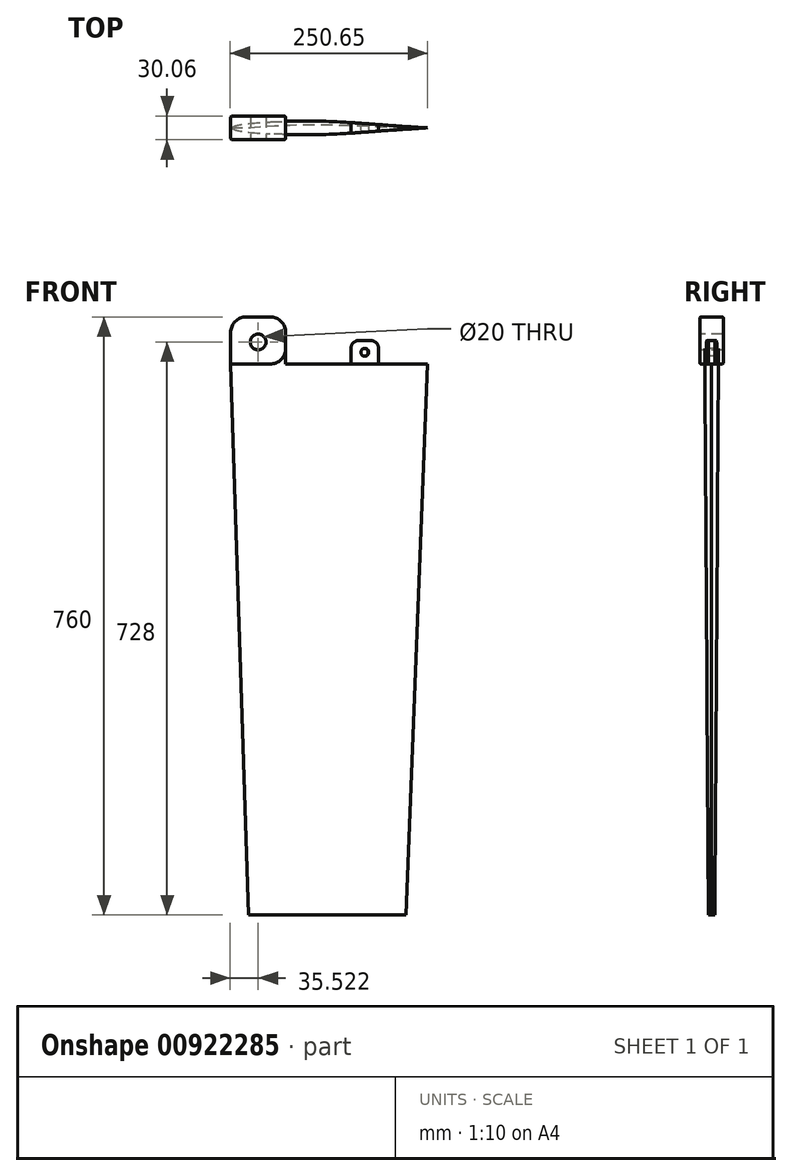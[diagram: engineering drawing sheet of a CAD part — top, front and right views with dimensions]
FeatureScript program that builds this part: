
annotation { "Feature Type Name" : "Feature", "Feature Type Description" : "" }
export const myFeature = defineFeature(function(context is Context, id is Id, definition is map)
    precondition{}
    {
        {
            var Q0;
            Q0=qCreatedBy(makeId("Top.planeOp"),FACE);
            var sketch = newSketch(context, id + "F0", { "sketchPlane" : qUnion([Q0])});
            skLineSegment(sketch, "E0", {"start": v(-132.78, 0) * mm, "end": v(117.22, 0) * mm});
            skFitSpline(sketch, "E1", {"points": [v(-132.78, 0) * mm, v(-121.8, 3.87) * mm, v(-98.61, 6.61) * mm, v(-16.83, 8.44) * mm, v(117.22, 0) * mm], "startDerivative": vector(116.96, 62.15) * mm, "endDerivative": vector(499.98, -28.84) * mm});
            skSolve(sketch);
        }
        {
            var Q0;
            Q0=qCreatedBy(makeId("Top.planeOp"),FACE);
            cPlane(context, id + "F1", {"entities" : qUnion([Q0]), "cplaneType" : CPlaneType.OFFSET, "offset" : 700 * mm, "oppositeDirection" : true, "width" : 150 * mm, "height" : 150 * mm});
        }
        {
            var Q0;
            Q0=qCreatedBy(id+"F1.planeOp",FACE);
            var sketch = newSketch(context, id + "F2", { "sketchPlane" : qUnion([Q0])});
            skLineSegment(sketch, "E2", {"start": v(-110.06, 0) * mm, "end": v(89.94, 0) * mm});
            skFitSpline(sketch, "E3", {"points": [v(-110.06, 0) * mm, v(-86.84, 2.4) * mm, v(-18.9, 4.12) * mm, v(30.9, 2.84) * mm, v(89.94, 0) * mm], "startDerivative": vector(17.15, 11.43) * mm, "endDerivative": vector(201.05, -10.2) * mm});
            skSolve(sketch);
        }
        {
            var Q0;
            Q0=makeQuery(id+"F0.imprint","IMPRINT",FACE,{"disambiguationData":[TD([[makeQuery(id+"F0.imprint","IMPRINT",EDGE,{"derivedFrom":sQuery(id+"F0.wireOp",EDGE,"E0")}),1.0]])]});
            var Q1;
            Q1=makeQuery(id+"F2.imprint","IMPRINT",FACE,{"disambiguationData":[TD([[makeQuery(id+"F2.imprint","IMPRINT",EDGE,{"derivedFrom":sQuery(id+"F2.wireOp",EDGE,"E2")}),1.0]])]});
            loft(context, id + "F3", {"sheetProfilesArray" : [{ "sheetProfileEntities" : qUnion([Q0]) }, { "sheetProfileEntities" : qUnion([Q1]) }]});
        }
        {
            var Q0;
            Q0=makeQuery(id+"F3.opLoft","SWEPT_BODY",BODY,{"disambiguationData":[OSD([makeQuery(id+"F0.imprint","IMPRINT",FACE,{"disambiguationData":[TD([[makeQuery(id+"F0.imprint","IMPRINT",EDGE,{"derivedFrom":sQuery(id+"F0.wireOp",EDGE,"E0")}),1.0]])]}),makeQuery(id+"F2.imprint","IMPRINT",FACE,{"disambiguationData":[TD([[makeQuery(id+"F2.imprint","IMPRINT",EDGE,{"derivedFrom":sQuery(id+"F2.wireOp",EDGE,"E2")}),1.0]])]})])]});
            var Q1;
            {var subQ0=sQuery(id+"F2.wireOp",EDGE,"E2");var subQ1=sQuery(id+"F2.wireOp",EDGE,"E3");var subQ2=sQuery(id+"F0.wireOp",EDGE,"E0");var subQ3=sQuery(id+"F0.wireOp",EDGE,"E1");Q1=makeQuery(id+"F3.opLoft","SWEPT_FACE",FACE,{"disambiguationData":[OSD([subQ2,subQ3,subQ0,subQ1]),TDD([makeQuery(id+"F0.imprint","INTERSECT",VERTEX,{"disambiguationData":[OD(0.0)],"derivedFrom":[subQ2,subQ3]}),makeQuery(id+"F0.imprint","INTERSECT",VERTEX,{"disambiguationData":[OD(1.0)],"derivedFrom":[subQ2,subQ3]}),makeQuery(id+"F0.imprint","IMPRINT",EDGE,{"derivedFrom":subQ2}),makeQuery(id+"F2.imprint","INTERSECT",VERTEX,{"disambiguationData":[OD(0.0)],"derivedFrom":[subQ0,subQ1]}),makeQuery(id+"F2.imprint","INTERSECT",VERTEX,{"disambiguationData":[OD(1.0)],"derivedFrom":[subQ0,subQ1]}),makeQuery(id+"F2.imprint","IMPRINT",EDGE,{"derivedFrom":subQ0})])]});}
            mirror(context, id + "F4", {"operationType" : NewBodyOperationType.ADD, "entities" : qUnion([Q0]), "mirrorPlane" : qUnion([Q1])});
        }
        {
            var Q0;
            {var subQ0=makeQuery(id+"F3.opLoft","CAP_FACE",FACE,{"disambiguationData":[OSD([makeQuery(id+"F0.imprint","IMPRINT",FACE,{"disambiguationData":[TD([[makeQuery(id+"F0.imprint","IMPRINT",EDGE,{"derivedFrom":sQuery(id+"F0.wireOp",EDGE,"E0")}),1.0]])]})])],"isStart":true});Q0=makeQuery(id+"F4.boolean.opBoolean","MERGE",FACE,{"derivedFrom":[subQ0,makeQuery(id+"F4.opPattern","COPY",FACE,{"derivedFrom":subQ0,"instanceName":"1"})]});}
            var sketch = newSketch(context, id + "F5", { "sketchPlane" : qUnion([Q0])});
            skLineSegment(sketch, "E4.bottom", {"start": v(-132.9, 15) * mm, "end": v(-62.9, 15) * mm});
            skLineSegment(sketch, "E4.top", {"start": v(-132.9, -15.06) * mm, "end": v(-62.9, -15.06) * mm});
            skLineSegment(sketch, "E4.left", {"start": v(-132.9, 15) * mm, "end": v(-132.9, -15.06) * mm});
            skLineSegment(sketch, "E4.right", {"start": v(-62.9, 15) * mm, "end": v(-62.9, -15.06) * mm});
            skSolve(sketch);
        }
        {
            var Q0;
            Q0 = qSketchRegion(id + "F5", true);
            extrude(context, id + "F6", {"entities" : qUnion([Q0]), "operationType" : NewBodyOperationType.ADD, "depth" : 60 * mm, "offsetDistance" : 25 * mm});
        }
        {
            var Q0;
            Q0=makeQuery(id+"F6.opExtrude","CAP_EDGE",EDGE,{"disambiguationData":[OSD([sQuery(id+"F5.wireOp",EDGE,"E4.left")])],"isStart":false});
            var Q1;
            Q1=makeQuery(id+"F6.opExtrude","CAP_EDGE",EDGE,{"disambiguationData":[OSD([sQuery(id+"F5.wireOp",EDGE,"E4.right")])],"isStart":false});
            fillet(context, id + "F7", {"entities" : qUnion([Q0, Q1]), "radius" : 20 * mm, "tangentPropagation" : true, "allowEdgeOverflow" : false});
        }
        {
            var Q0;
            Q0=makeQuery(id+"F6.opExtrude","SWEPT_EDGE",EDGE,{"disambiguationData":[OSD([sQuery(id+"F5.wireOp",EDGE,"E4.top"),sQuery(id+"F5.wireOp",EDGE,"E4.left")])]});
            var Q1;
            Q1=makeQuery(id+"F6.opExtrude","SWEPT_EDGE",EDGE,{"disambiguationData":[OSD([sQuery(id+"F5.wireOp",EDGE,"E4.bottom"),sQuery(id+"F5.wireOp",EDGE,"E4.left")])]});
            var Q2;
            Q2=makeQuery(id+"F6.opExtrude","CAP_EDGE",EDGE,{"disambiguationData":[OSD([sQuery(id+"F5.wireOp",EDGE,"E4.top")])],"isStart":true});
            var Q3;
            Q3=makeQuery(id+"F6.opExtrude","CAP_EDGE",EDGE,{"disambiguationData":[OSD([sQuery(id+"F5.wireOp",EDGE,"E4.bottom")])],"isStart":true});
            fillet(context, id + "F8", {"entities" : qUnion([Q0, Q1, Q2, Q3]), "radius" : 2 * mm, "tangentPropagation" : true, "allowEdgeOverflow" : false});
        }
        {
            var Q0;
            Q0=makeQuery(id+"F6.opExtrude","SWEPT_FACE",FACE,{"disambiguationData":[OSD([sQuery(id+"F5.wireOp",EDGE,"E4.top")])]});
            var sketch = newSketch(context, id + "F9", { "sketchPlane" : qUnion([Q0])});
            skCircle(sketch, "E5", {"center": v(-97.9, 28) * mm, "radius": 10 * mm});
            skSolve(sketch);
        }
        {
            var Q0;
            Q0 = qSketchRegion(id + "F9", true);
            extrude(context, id + "F10", {"entities" : qUnion([Q0]), "operationType" : NewBodyOperationType.REMOVE, "endBound" : BoundingType.THROUGH_ALL, "oppositeDirection" : true, "depth" : 25 * mm, "offsetDistance" : 25 * mm});
        }
        {
            var Q0;
            {var subQ0=makeQuery(id+"F3.opLoft","CAP_FACE",FACE,{"disambiguationData":[OSD([makeQuery(id+"F0.imprint","IMPRINT",FACE,{"disambiguationData":[TD([[makeQuery(id+"F0.imprint","IMPRINT",EDGE,{"derivedFrom":sQuery(id+"F0.wireOp",EDGE,"E0")}),1.0]])]})])],"isStart":true});var subQ1=sQuery(id+"F5.wireOp",EDGE,"E4.right");Q0=makeQuery(id+"F6.boolean.opBoolean","SPLIT",EDGE,{"disambiguationData":[topologyDisambiguationEdgeConnected([subQ0,makeQuery(id+"F4.opPattern","COPY",FACE,{"derivedFrom":subQ0,"instanceName":"1"}),makeQuery(id+"F6.opExtrude","SWEPT_FACE",FACE,{"disambiguationData":[OSD([subQ1])]})])],"derivedFrom":makeQuery(id+"F6.opExtrude","CAP_EDGE",EDGE,{"disambiguationData":[OSD([subQ1])],"isStart":true})});}
            fillet(context, id + "F11", {"entities" : qUnion([Q0]), "radius" : 20 * mm, "tangentPropagation" : true, "allowEdgeOverflow" : false});
        }
        {
            var Q0;
            {var subQ0=makeQuery(id+"F3.opLoft","CAP_FACE",FACE,{"disambiguationData":[OSD([makeQuery(id+"F0.imprint","IMPRINT",FACE,{"disambiguationData":[TD([[makeQuery(id+"F0.imprint","IMPRINT",EDGE,{"derivedFrom":sQuery(id+"F0.wireOp",EDGE,"E0")}),1.0]])]})])],"isStart":true});Q0=makeQuery(id+"F4.boolean.opBoolean","MERGE",FACE,{"derivedFrom":[subQ0,makeQuery(id+"F4.opPattern","COPY",FACE,{"derivedFrom":subQ0,"instanceName":"1"})]});}
            var sketch = newSketch(context, id + "F12", { "sketchPlane" : qUnion([Q0])});
            skLineSegment(sketch, "E6", {"start": v(20, 6.68) * mm, "end": v(20, -6.68) * mm});
            skLineSegment(sketch, "E7", {"start": v(20, -6.68) * mm, "end": v(54.9, -4.15) * mm});
            skLineSegment(sketch, "E8", {"start": v(54.9, -4.15) * mm, "end": v(54.9, 4.15) * mm});
            skLineSegment(sketch, "E9", {"start": v(54.9, 4.15) * mm, "end": v(20, 6.68) * mm});
            skSolve(sketch);
        }
        {
            var Q0;
            Q0 = qSketchRegion(id + "F12", true);
            extrude(context, id + "F13", {"entities" : qUnion([Q0]), "operationType" : NewBodyOperationType.ADD, "depth" : 30 * mm, "offsetDistance" : 25 * mm});
        }
        {
            var Q0;
            Q0=makeQuery(id+"F13.opExtrude","CAP_EDGE",EDGE,{"disambiguationData":[OSD([sQuery(id+"F12.wireOp",EDGE,"E6")])],"isStart":false});
            var Q1;
            Q1=makeQuery(id+"F13.opExtrude","CAP_EDGE",EDGE,{"disambiguationData":[OSD([sQuery(id+"F12.wireOp",EDGE,"E8")])],"isStart":false});
            fillet(context, id + "F14", {"entities" : qUnion([Q0, Q1]), "radius" : 10 * mm, "tangentPropagation" : true, "allowEdgeOverflow" : false});
        }
        {
            var Q0;
            Q0=makeQuery(id+"F13.opExtrude","SWEPT_FACE",FACE,{"disambiguationData":[OSD([sQuery(id+"F12.wireOp",EDGE,"E7")])]});
            var sketch = newSketch(context, id + "F15", { "sketchPlane" : qUnion([Q0])});
            skCircle(sketch, "E10", {"center": v(37, 15) * mm, "radius": 5 * mm});
            skSolve(sketch);
        }
        {
            var Q0;
            Q0=makeQuery(id+"F15.imprint","IMPRINT",FACE,{"disambiguationData":[TD([[makeQuery(id+"F15.imprint","IMPRINT",EDGE,{"derivedFrom":sQuery(id+"F15.wireOp",EDGE,"E10")}),1.0]])]});
            extrude(context, id + "F16", {"entities" : qUnion([Q0]), "operationType" : NewBodyOperationType.REMOVE, "endBound" : BoundingType.THROUGH_ALL, "oppositeDirection" : true, "depth" : 25 * mm, "offsetDistance" : 25 * mm});
        }
    });
